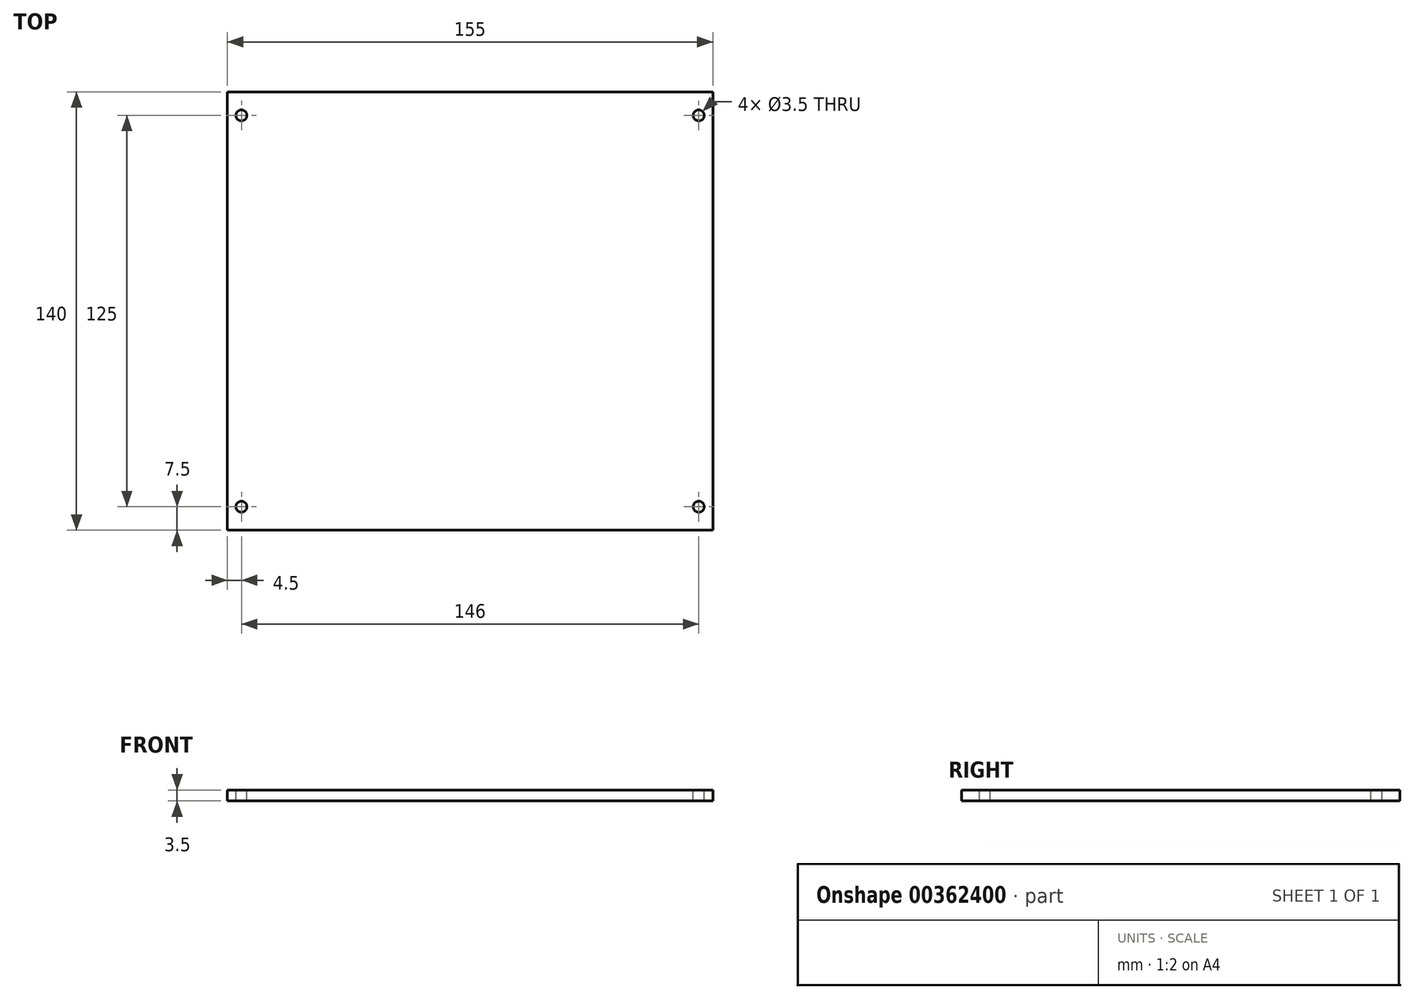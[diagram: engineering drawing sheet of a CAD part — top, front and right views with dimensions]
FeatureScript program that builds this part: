
annotation { "Feature Type Name" : "Feature", "Feature Type Description" : "" }
export const myFeature = defineFeature(function(context is Context, id is Id, definition is map)
    precondition{}
    {
        {
            var Q0;
            Q0=qCreatedBy(makeId("Top.planeOp"),FACE);
            var sketch = newSketch(context, id + "F0", { "sketchPlane" : qUnion([Q0])});
            skLineSegment(sketch, "E0.bottom", {"start": v(77.5, -70) * mm, "end": v(-77.5, -70) * mm});
            skLineSegment(sketch, "E0.top", {"start": v(77.5, 70) * mm, "end": v(-77.5, 70) * mm});
            skLineSegment(sketch, "E0.left", {"start": v(77.5, -70) * mm, "end": v(77.5, 70) * mm});
            skLineSegment(sketch, "E0.right", {"start": v(-77.5, -70) * mm, "end": v(-77.5, 70) * mm});
            skPoint(sketch, "E0.middle", {"position": v(0, 0) * mm});
            skSolve(sketch);
        }
        {
            var Q0;
            Q0=qSketchRegion(id+"F0",true);
            extrude(context, id + "F1", {"entities" : qUnion([Q0]), "depth" : 3.5 * mm});
        }
        {
            var Q0;
            Q0=makeQuery(id+"F1.opExtrude","CAP_FACE",FACE,{"disambiguationData":[OSD([sQuery(id+"F0.wireOp",EDGE,"E0.bottom"),sQuery(id+"F0.wireOp",EDGE,"E0.top"),sQuery(id+"F0.wireOp",EDGE,"E0.left"),sQuery(id+"F0.wireOp",EDGE,"E0.right")])],"isStart":false});
            var sketch = newSketch(context, id + "F2", { "sketchPlane" : qUnion([Q0])});
            skCircle(sketch, "E1", {"center": v(-73, 62.5) * mm, "radius": 1.75 * mm});
            skCircle(sketch, "E2", {"center": v(73, 62.5) * mm, "radius": 1.75 * mm});
            skLineSegment(sketch, "E3", {"start": v(0, 0) * mm, "end": v(-44.5, 0) * mm});
            skCircle(sketch, "E4.MirrorC", {"center": v(-73, -62.5) * mm, "radius": 1.75 * mm});
            skCircle(sketch, "E5.MirrorC", {"center": v(73, -62.5) * mm, "radius": 1.75 * mm});
            skSolve(sketch);
        }
        {
            var Q0;
            Q0=qSketchRegion(id+"F2",true);
            extrude(context, id + "F3", {"entities" : qUnion([Q0]), "operationType" : NewBodyOperationType.REMOVE, "endBound" : BoundingType.THROUGH_ALL, "oppositeDirection" : true, "depth" : 25 * mm});
        }
    });
